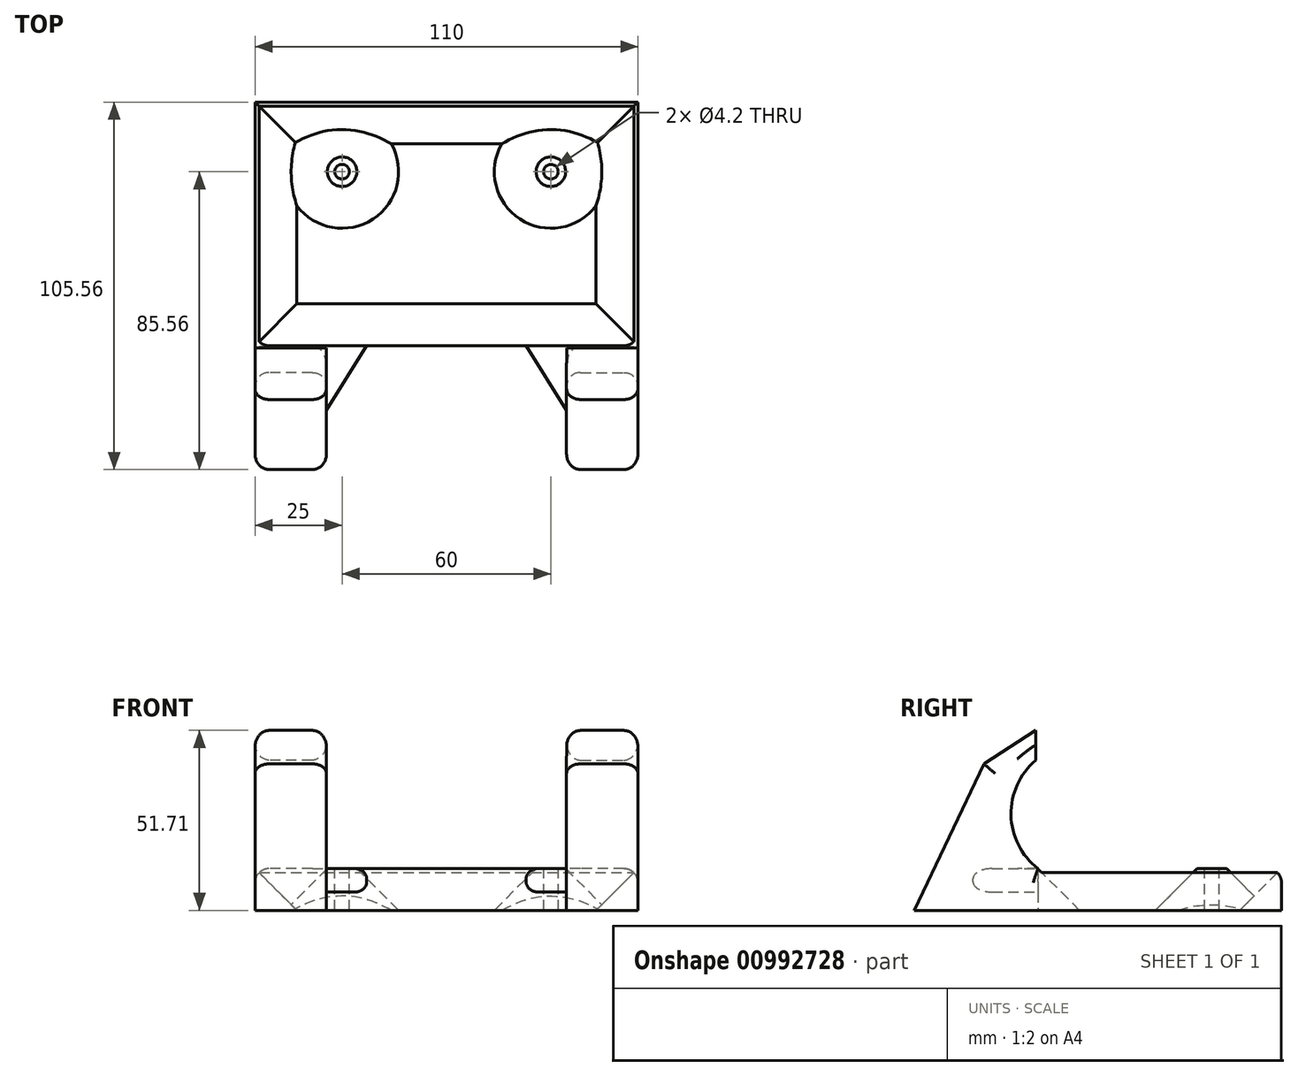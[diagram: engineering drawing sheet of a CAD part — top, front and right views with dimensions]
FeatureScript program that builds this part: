
annotation { "Feature Type Name" : "Feature", "Feature Type Description" : "" }
export const myFeature = defineFeature(function(context is Context, id is Id, definition is map)
    precondition{}
    {
        {
            var Q0;
            Q0=qCreatedBy(makeId("Top.planeOp"),FACE);
            var sketch = newSketch(context, id + "F0", { "sketchPlane" : qUnion([Q0])});
            skLineSegment(sketch, "E0.bottom", {"start": v(55, -35) * mm, "end": v(-55, -35) * mm});
            skLineSegment(sketch, "E0.top", {"start": v(55, 35) * mm, "end": v(-55, 35) * mm});
            skLineSegment(sketch, "E0.left", {"start": v(55, -35) * mm, "end": v(55, 35) * mm});
            skLineSegment(sketch, "E0.right", {"start": v(-55, -35) * mm, "end": v(-55, 35) * mm});
            skPoint(sketch, "E0.middle", {"position": v(0, 0) * mm});
            skSolve(sketch);
        }
        {
            var Q0;
            Q0=qSketchRegion(id+"F0",true);
            extrude(context, id + "F1", {"entities" : qUnion([Q0]), "depth" : 12 * mm, "offsetDistance" : 25 * mm});
        }
        {
            var Q0;
            Q0=makeQuery(id+"F1.opExtrude","CAP_FACE",FACE,{"disambiguationData":[OSD([sQuery(id+"F0.wireOp",EDGE,"E0.bottom"),sQuery(id+"F0.wireOp",EDGE,"E0.top"),sQuery(id+"F0.wireOp",EDGE,"E0.left"),sQuery(id+"F0.wireOp",EDGE,"E0.right")])],"isStart":false});
            var sketch = newSketch(context, id + "F2", { "sketchPlane" : qUnion([Q0])});
            skLineSegment(sketch, "E1", {"start": v(0, 0) * mm, "end": v(-30, 0) * mm, "construction": true});
            skLineSegment(sketch, "E2", {"start": v(-30, 0) * mm, "end": v(-30, 15) * mm, "construction": true});
            skLineSegment(sketch, "E3", {"start": v(0, 0) * mm, "end": v(0, 35) * mm, "construction": true});
            skCircle(sketch, "E4", {"center": v(-30, 15) * mm, "radius": 4.25 * mm});
            skCircle(sketch, "E5.MirrorC", {"center": v(30, 15) * mm, "radius": 4.25 * mm});
            skCircle(sketch, "E6", {"center": v(-30, 15) * mm, "radius": 2.1 * mm});
            skCircle(sketch, "E7", {"center": v(30, 15) * mm, "radius": 2.1 * mm});
            skSolve(sketch);
        }
        {
            var Q0;
            Q0=makeQuery(id+"F1.opExtrude","SWEPT_FACE",FACE,{"disambiguationData":[OSD([sQuery(id+"F0.wireOp",EDGE,"E0.right")])]});
            var sketch = newSketch(context, id + "F3", { "sketchPlane" : qUnion([Q0])});
            skLineSegment(sketch, "E8", {"start": v(35.66, 43.15) * mm, "end": v(35.66, 51.7) * mm});
            skLineSegment(sketch, "E9", {"start": v(35.66, 51.7) * mm, "end": v(50.47, 42.08) * mm});
            skLineSegment(sketch, "E10", {"start": v(50.47, 42.08) * mm, "end": v(70.56, 0) * mm});
            skLineSegment(sketch, "E11", {"start": v(61.36, 0) * mm, "end": v(70.56, 0) * mm});
            skArc(sketch, "E12", {"start": v(35, 12) * mm, "mid": v(42.7, 27.42) * mm, "end": v(35.66, 43.15) * mm});
            skLineSegment(sketch, "E13", {"start": v(35, 0) * mm, "end": v(35, 12) * mm});
            skLineSegment(sketch, "E14", {"start": v(35, 0) * mm, "end": v(61.36, 0) * mm});
            skSolve(sketch);
        }
        {
            var Q0;
            Q0=qSketchRegion(id+"F3",true);
            var Q1;
            Q1=makeQuery(id+"F3.imprint","IMPRINT",FACE,{"disambiguationData":[TD([[makeQuery(id+"F3.imprint","IMPRINT",EDGE,{"derivedFrom":sQuery(id+"F3.wireOp",EDGE,"7Pwc14p4-GtLF-zbwn-A3yy-zM8IYJwOLAtm")}),-1.0]])]});
            extrude(context, id + "F4", {"entities" : qUnion([Q0, Q1]), "operationType" : NewBodyOperationType.ADD, "oppositeDirection" : true, "depth" : 15.5 * mm, "offsetDistance" : 25 * mm});
        }
        {
            var Q0;
            Q0=makeQuery(id+"F2.imprint","IMPRINT",FACE,{"disambiguationData":[TD([[makeQuery(id+"F2.imprint","IMPRINT",EDGE,{"derivedFrom":sQuery(id+"F2.wireOp",EDGE,"E4")}),-1.0]])]});
            var sketch = newSketch(context, id + "F5", { "sketchPlane" : qUnion([Q0])});
            skLineSegment(sketch, "E15.0", {"start": v(55, -35) * mm, "end": v(-39.5, -35) * mm});
            skLineSegment(sketch, "E16", {"start": v(-39.5, -35) * mm, "end": v(-39.5, -45) * mm});
            skPoint(sketch, "E17.0", {"position": v(-39.5, -41.17) * mm});
            skLineSegment(sketch, "E18", {"start": v(-39.78, -62.08) * mm, "end": v(-22.92, -35) * mm});
            skLineSegment(sketch, "E19", {"start": v(-39.78, -62.08) * mm, "end": v(-39.5, -45) * mm});
            skSolve(sketch);
        }
        {
            var Q0;
            Q0=makeQuery(id+"F4.opExtrude","CAP_FACE",FACE,{"disambiguationData":[OSD([sQuery(id+"F0.wireOp",EDGE,"E0.bottom"),sQuery(id+"F0.wireOp",EDGE,"E0.right"),sQuery(id+"F3.wireOp",EDGE,"7Pwc14p4-GtLF-zbwn-A3yy-zM8IYJwOLAtm"),sQuery(id+"F3.wireOp",EDGE,"E8"),sQuery(id+"F3.wireOp",EDGE,"E9"),sQuery(id+"F3.wireOp",EDGE,"E10"),sQuery(id+"F3.wireOp",EDGE,"gI4tzJGO-jobw-9Nqk-Fxfu-Kbz7aSWXKX2u"),sQuery(id+"F3.wireOp",EDGE,"E11")])],"isStart":false});
            var sketch = newSketch(context, id + "F6", { "sketchPlane" : qUnion([Q0])});
            skPoint(sketch, "E20.0", {"position": v(-35, 0) * mm});
            skPoint(sketch, "E21.0", {"position": v(-45, 12) * mm});
            skArc(sketch, "E22", {"start": v(-35, 0) * mm, "mid": v(-49.96, 7.21) * mm, "end": v(-66.56, 7.02) * mm});
            skLineSegment(sketch, "E23", {"start": v(-66.56, 7.02) * mm, "end": v(-70.56, 0) * mm});
            skLineSegment(sketch, "E24", {"start": v(-70.56, 0) * mm, "end": v(-35, 0) * mm});
            skLineSegment(sketch, "E25", {"start": v(-35, 5) * mm, "end": v(-35, 0) * mm});
            skLineSegment(sketch, "E26", {"start": v(-45, 12) * mm, "end": v(-66.45, 15.34) * mm});
            skLineSegment(sketch, "E27", {"start": v(-66.45, 15.34) * mm, "end": v(-66.56, 7.02) * mm});
            skLineSegment(sketch, "E28", {"start": v(-45, 12) * mm, "end": v(-35, 0) * mm});
            skSolve(sketch);
        }
        {
            var Q0;
            {var subQ0=sQuery(id+"F5.wireOp",EDGE,"E16");Q0=makeQuery(id+"F5.imprint","IMPRINT",FACE,{"disambiguationData":[TD([[makeQuery(id+"F5.imprint","IMPRINT",EDGE,{"derivedFrom":subQ0}),1.0]])]});}
            extrude(context, id + "F7", {"entities" : qUnion([Q0]), "operationType" : NewBodyOperationType.ADD, "oppositeDirection" : true, "depth" : 6.75 * mm, "offsetDistance" : 25 * mm});
        }
        {
            var Q0;
            {var subQ0=sQuery(id+"F6.wireOp",EDGE,"E25");Q0=makeQuery(id+"F6.imprint","IMPRINT",FACE,{"disambiguationData":[TD([[makeQuery(id+"F6.imprint","IMPRINT",EDGE,{"derivedFrom":subQ0}),-1.0]])]});}
            extrude(context, id + "F8", {"entities" : qUnion([Q0]), "operationType" : NewBodyOperationType.ADD, "depth" : 5 * mm, "offsetDistance" : 25 * mm});
        }
        {
            var Q0;
            {var subQ2=sQuery(id+"F6.wireOp",EDGE,"E22");Q0=makeQuery(id+"F6.imprint","IMPRINT",FACE,{"disambiguationData":[TD([[makeQuery(id+"F6.imprint","IMPRINT",EDGE,{"derivedFrom":subQ2}),-1.0]])]});}
            var Q1;
            Q1=makeQuery(id+"F6.imprint","IMPRINT",FACE,{"disambiguationData":[TD([[makeQuery(id+"F6.imprint","IMPRINT",EDGE,{"derivedFrom":sQuery(id+"F6.wireOp",EDGE,"E22")}),1.0]])]});
            var Q2;
            {var subQ0=sQuery(id+"F6.wireOp",EDGE,"E23");Q2=makeQuery(id+"F6.imprint","IMPRINT",FACE,{"disambiguationData":[TD([[makeQuery(id+"F6.imprint","IMPRINT",EDGE,{"derivedFrom":subQ0}),-1.0]])]});}
            extrude(context, id + "F9", {"entities" : qUnion([Q0, Q1, Q2]), "operationType" : NewBodyOperationType.ADD, "depth" : 5 * mm, "offsetDistance" : 25 * mm});
        }
        {
            var Q0;
            Q0=makeQuery(id+"F4.opExtrude","CAP_EDGE",EDGE,{"disambiguationData":[OSD([sQuery(id+"F3.wireOp",EDGE,"7Pwc14p4-GtLF-zbwn-A3yy-zM8IYJwOLAtm")])],"isStart":true});
            var Q1;
            Q1=makeQuery(id+"F4.opExtrude","CAP_EDGE",EDGE,{"disambiguationData":[OSD([sQuery(id+"F3.wireOp",EDGE,"E10")])],"isStart":true});
            var Q2;
            Q2=makeQuery(id+"F4.opExtrude","CAP_EDGE",EDGE,{"disambiguationData":[OSD([sQuery(id+"F3.wireOp",EDGE,"E10")])],"isStart":false});
            var Q3;
            Q3=makeQuery(id+"F4.opExtrude","CAP_EDGE",EDGE,{"disambiguationData":[OSD([sQuery(id+"F3.wireOp",EDGE,"E9")])],"isStart":true});
            var Q4;
            Q4=makeQuery(id+"F4.opExtrude","CAP_EDGE",EDGE,{"disambiguationData":[OSD([sQuery(id+"F3.wireOp",EDGE,"E9")])],"isStart":false});
            var Q5;
            Q5=makeQuery(id+"F1.opExtrude","CAP_EDGE",EDGE,{"disambiguationData":[OSD([sQuery(id+"F0.wireOp",EDGE,"E0.top")])],"isStart":false});
            var Q6;
            Q6=makeQuery(id+"F1.opExtrude","CAP_EDGE",EDGE,{"disambiguationData":[OSD([sQuery(id+"F0.wireOp",EDGE,"E0.left")])],"isStart":false});
            var Q7;
            Q7=makeQuery(id+"F4.opExtrude","CAP_EDGE",EDGE,{"disambiguationData":[OSD([sQuery(id+"F3.wireOp",EDGE,"7Pwc14p4-GtLF-zbwn-A3yy-zM8IYJwOLAtm")])],"isStart":false});
            var Q8;
            Q8=makeQuery(id+"F8.opExtrude","CAP_EDGE",EDGE,{"disambiguationData":[OSD([sQuery(id+"F3.wireOp",EDGE,"E10")])],"isStart":false});
            var Q9;
            Q9=makeQuery(id+"F8.opExtrude","CAP_EDGE",EDGE,{"disambiguationData":[OSD([sQuery(id+"F3.wireOp",EDGE,"E9")])],"isStart":false});
            var Q10;
            Q10=makeQuery(id+"F1.opExtrude","CAP_EDGE",EDGE,{"disambiguationData":[OSD([sQuery(id+"F0.wireOp",EDGE,"E0.right")])],"isStart":false});
            var Q11;
            Q11=makeQuery(id+"F4.opExtrude","CAP_EDGE",EDGE,{"disambiguationData":[OSD([sQuery(id+"F3.wireOp",EDGE,"E12")])],"isStart":true});
            var Q12;
            Q12=makeQuery(id+"F8.opExtrude","CAP_EDGE",EDGE,{"disambiguationData":[OSD([sQuery(id+"F3.wireOp",EDGE,"E12")])],"isStart":false});
            fillet(context, id + "F10", {"entities" : qUnion([Q0, Q1, Q2, Q3, Q4, Q5, Q6, Q7, Q8, Q9, Q10, Q11, Q12]), "radius" : 4 * mm, "tangentPropagation" : true, "allowEdgeOverflow" : false});
        }
        {
            var Q0;
            Q0=makeQuery(id+"F2.imprint","IMPRINT",FACE,{"disambiguationData":[TD([[makeQuery(id+"F2.imprint","IMPRINT",EDGE,{"derivedFrom":sQuery(id+"F2.wireOp",EDGE,"E4")}),1.0]])]});
            var Q1;
            Q1=makeQuery(id+"F2.imprint","IMPRINT",FACE,{"disambiguationData":[TD([[makeQuery(id+"F2.imprint","IMPRINT",EDGE,{"derivedFrom":sQuery(id+"F2.wireOp",EDGE,"E6")}),1.0]])]});
            var Q2;
            Q2=makeQuery(id+"F2.imprint","IMPRINT",FACE,{"disambiguationData":[TD([[makeQuery(id+"F2.imprint","IMPRINT",EDGE,{"derivedFrom":sQuery(id+"F2.wireOp",EDGE,"E5.MirrorC")}),-1.0]])]});
            var Q3;
            Q3=makeQuery(id+"F2.imprint","IMPRINT",FACE,{"disambiguationData":[TD([[makeQuery(id+"F2.imprint","IMPRINT",EDGE,{"derivedFrom":sQuery(id+"F2.wireOp",EDGE,"E7")}),1.0]])]});
            extrude(context, id + "F11", {"entities" : qUnion([Q0, Q1, Q2, Q3]), "operationType" : NewBodyOperationType.REMOVE, "oppositeDirection" : true, "depth" : 25 * mm, "offsetDistance" : 25 * mm, "hasDraft" : true, "draftAngle" : 45 * degree, "draftPullDirection" : true});
        }
        {
            var Q0;
            Q0=makeQuery(id+"F2.imprint","IMPRINT",FACE,{"disambiguationData":[TD([[makeQuery(id+"F2.imprint","IMPRINT",EDGE,{"derivedFrom":sQuery(id+"F2.wireOp",EDGE,"E7")}),1.0]])]});
            var Q1;
            Q1=makeQuery(id+"F2.imprint","IMPRINT",FACE,{"disambiguationData":[TD([[makeQuery(id+"F2.imprint","IMPRINT",EDGE,{"derivedFrom":sQuery(id+"F2.wireOp",EDGE,"E6")}),1.0]])]});
            extrude(context, id + "F12", {"entities" : qUnion([Q0, Q1]), "operationType" : NewBodyOperationType.REMOVE, "oppositeDirection" : true, "depth" : 25 * mm, "offsetDistance" : 25 * mm});
        }
        {
            var Q0;
            Q0=makeQuery(id+"F1.opExtrude","SWEPT_BODY",BODY,{"disambiguationData":[OSD([sQuery(id+"F0.wireOp",EDGE,"E0.bottom"),sQuery(id+"F0.wireOp",EDGE,"E0.top"),sQuery(id+"F0.wireOp",EDGE,"E0.left"),sQuery(id+"F0.wireOp",EDGE,"E0.right")])]});
            var Q1;
            Q1=qCreatedBy(makeId("Right.planeOp"),FACE);
            mirror(context, id + "F13", {"operationType" : NewBodyOperationType.ADD, "entities" : qUnion([Q0]), "mirrorPlane" : qUnion([Q1])});
        }
        {
            var Q0;
            Q0=makeQuery(id+"F2.imprint","IMPRINT",FACE,{"disambiguationData":[TD([[makeQuery(id+"F2.imprint","IMPRINT",EDGE,{"derivedFrom":sQuery(id+"F2.wireOp",EDGE,"E4")}),-1.0]])]});
            var sketch = newSketch(context, id + "F14", { "sketchPlane" : qUnion([Q0])});
            skText(sketch, "E29", { "text": "CSULB", "fontName": "AllertaStencil-Regular.ttf"});
            const initialGuessF14  = {"E29": [-0.025, -0.01607, 1, 0, 0.01153]};
            skSetInitialGuess(sketch, initialGuessF14);
            skSolve(sketch);
        }
        {
            var Q0;
            Q0=qSketchRegion(id+"F14",true);
            extrude(context, id + "F15", {"entities" : qUnion([Q0]), "operationType" : NewBodyOperationType.REMOVE, "oppositeDirection" : true, "depth" : 1.5 * mm, "offsetDistance" : 25 * mm});
        }
        {
            var Q0;
            Q0=makeQuery(id+"F7.opExtrude","CAP_EDGE",EDGE,{"disambiguationData":[OSD([sQuery(id+"F5.wireOp",EDGE,"E18")])],"isStart":true});
            var Q1;
            Q1=makeQuery(id+"F7.opExtrude","CAP_EDGE",EDGE,{"disambiguationData":[OSD([sQuery(id+"F5.wireOp",EDGE,"E18")])],"isStart":false});
            var Q2;
            Q2=makeQuery(id+"F13.opPattern","COPY",EDGE,{"derivedFrom":makeQuery(id+"F7.opExtrude","CAP_EDGE",EDGE,{"disambiguationData":[OSD([sQuery(id+"F5.wireOp",EDGE,"E18")])],"isStart":false}),"instanceName":"1"});
            var Q3;
            Q3=makeQuery(id+"F13.opPattern","COPY",EDGE,{"derivedFrom":makeQuery(id+"F7.opExtrude","CAP_EDGE",EDGE,{"disambiguationData":[OSD([sQuery(id+"F5.wireOp",EDGE,"E18")])],"isStart":true}),"instanceName":"1"});
            fillet(context, id + "F16", {"entities" : qUnion([Q0, Q1, Q2, Q3]), "radius" : 2.9 * mm, "tangentPropagation" : true, "allowEdgeOverflow" : false});
        }
    });
